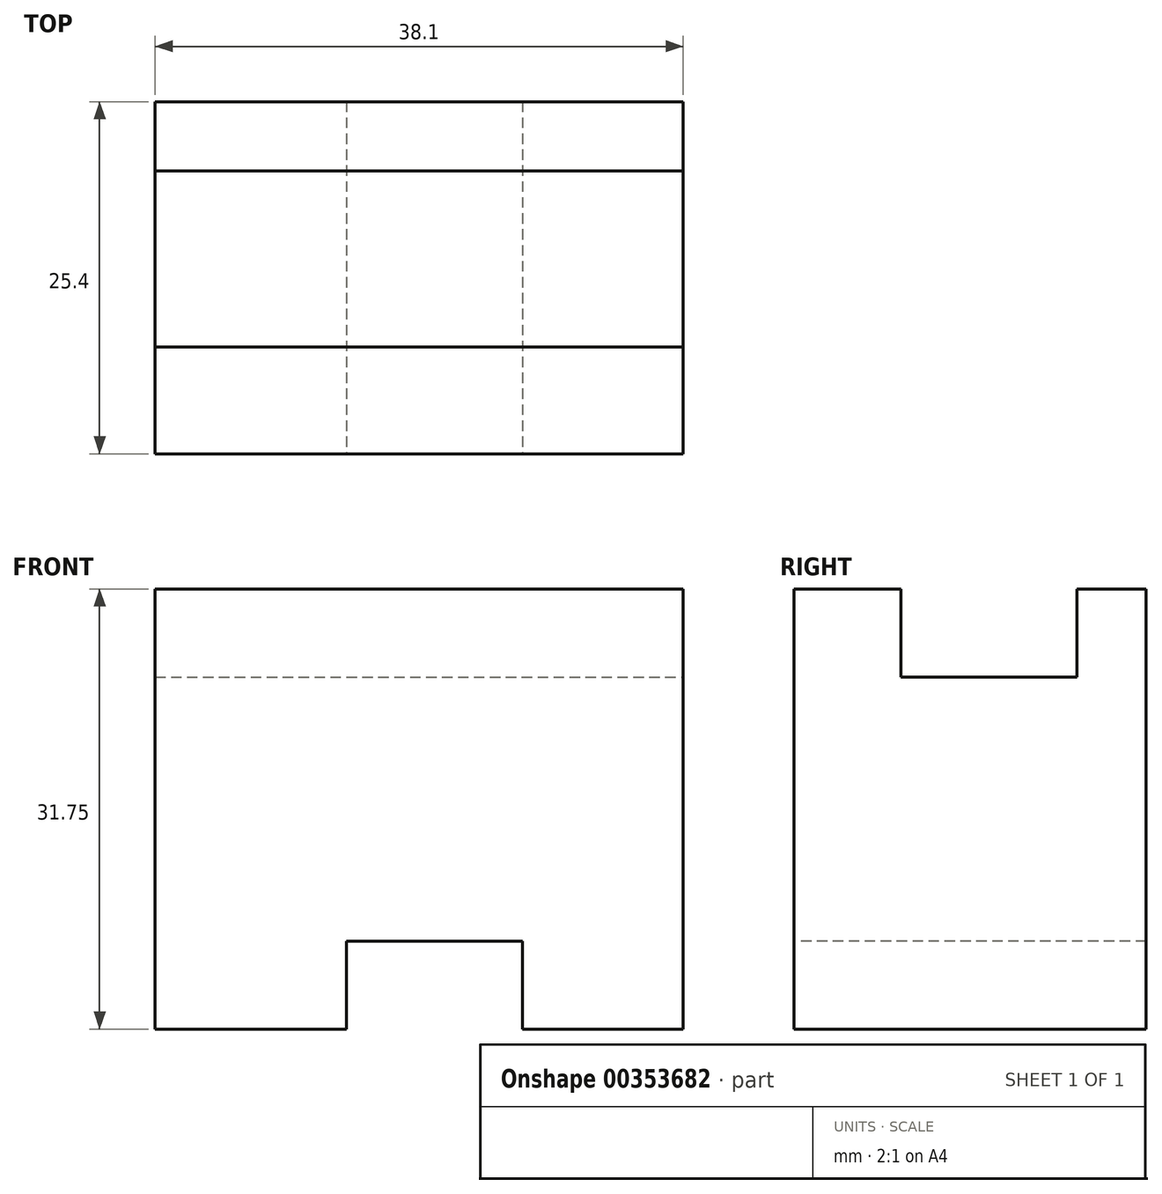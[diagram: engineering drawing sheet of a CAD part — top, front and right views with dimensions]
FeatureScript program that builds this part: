
annotation { "Feature Type Name" : "Feature", "Feature Type Description" : "" }
export const myFeature = defineFeature(function(context is Context, id is Id, definition is map)
    precondition{}
    {
        {
            var Q0;
            Q0=qCreatedBy(makeId("Front.planeOp"),FACE);
            var sketch = newSketch(context, id + "F0", { "sketchPlane" : qUnion([Q0])});
            skLineSegment(sketch, "E0", {"start": v(-24.65, 31.71) * mm, "end": v(13.45, 31.71) * mm});
            skLineSegment(sketch, "E1", {"start": v(-24.65, 31.71) * mm, "end": v(-24.65, -0.04) * mm});
            skLineSegment(sketch, "E2", {"start": v(-24.65, -0.04) * mm, "end": v(13.45, -0.04) * mm});
            skLineSegment(sketch, "E3", {"start": v(13.45, -0.04) * mm, "end": v(13.45, 31.71) * mm});
            skSolve(sketch);
        }
        {
            var Q0;
            Q0=makeQuery(id+"F0.imprint","IMPRINT",FACE,{"disambiguationData":[TD([[makeQuery(id+"F0.imprint","IMPRINT",EDGE,{"derivedFrom":sQuery(id+"F0.wireOp",EDGE,"E0")}),-1.0]])]});
            extrude(context, id + "F1", {"entities" : qUnion([Q0]), "depth" : 25.4 * mm});
        }
        {
            var Q0;
            Q0=makeQuery(id+"F1.opExtrude","SWEPT_FACE",FACE,{"disambiguationData":[OSD([sQuery(id+"F0.wireOp",EDGE,"E0")])]});
            var sketch = newSketch(context, id + "F2", { "sketchPlane" : qUnion([Q0])});
            skLineSegment(sketch, "E4", {"start": v(-24.65, -5) * mm, "end": v(13.45, -5) * mm});
            skLineSegment(sketch, "E5", {"start": v(13.45, -5) * mm, "end": v(13.45, -17.7) * mm});
            skLineSegment(sketch, "E6", {"start": v(13.45, -17.7) * mm, "end": v(-24.65, -17.7) * mm});
            skLineSegment(sketch, "E7", {"start": v(-24.65, -17.7) * mm, "end": v(-24.65, -5) * mm});
            skSolve(sketch);
        }
        {
            var Q0;
            Q0=makeQuery(id+"F2.imprint","IMPRINT",FACE,{"disambiguationData":[TD([[makeQuery(id+"F2.imprint","IMPRINT",EDGE,{"derivedFrom":sQuery(id+"F2.wireOp",EDGE,"E4")}),-1.0]])]});
            extrude(context, id + "F3", {"entities" : qUnion([Q0]), "operationType" : NewBodyOperationType.REMOVE, "oppositeDirection" : true, "depth" : 6.35 * mm});
        }
        {
            var Q0;
            Q0=makeQuery(id+"F1.opExtrude","CAP_FACE",FACE,{"disambiguationData":[OSD([sQuery(id+"F0.wireOp",EDGE,"E0"),sQuery(id+"F0.wireOp",EDGE,"E1"),sQuery(id+"F0.wireOp",EDGE,"E2"),sQuery(id+"F0.wireOp",EDGE,"E3")])],"isStart":false});
            var sketch = newSketch(context, id + "F4", { "sketchPlane" : qUnion([Q0])});
            skLineSegment(sketch, "E8", {"start": v(-10.84, -0.04) * mm, "end": v(-10.84, 6.31) * mm});
            skLineSegment(sketch, "E9", {"start": v(-10.84, 6.31) * mm, "end": v(1.86, 6.31) * mm});
            skLineSegment(sketch, "E10", {"start": v(1.86, 6.31) * mm, "end": v(1.86, -0.04) * mm});
            skSolve(sketch);
        }
        {
            var Q0;
            {var subQ0=sQuery(id+"F4.wireOp",EDGE,"E8");Q0=makeQuery(id+"F4.imprint","IMPRINT",FACE,{"disambiguationData":[TD([[makeQuery(id+"F4.imprint","IMPRINT",EDGE,{"derivedFrom":subQ0}),-1.0]])]});}
            extrude(context, id + "F5", {"entities" : qUnion([Q0]), "operationType" : NewBodyOperationType.REMOVE, "oppositeDirection" : true, "depth" : 25.4 * mm});
        }
    });
